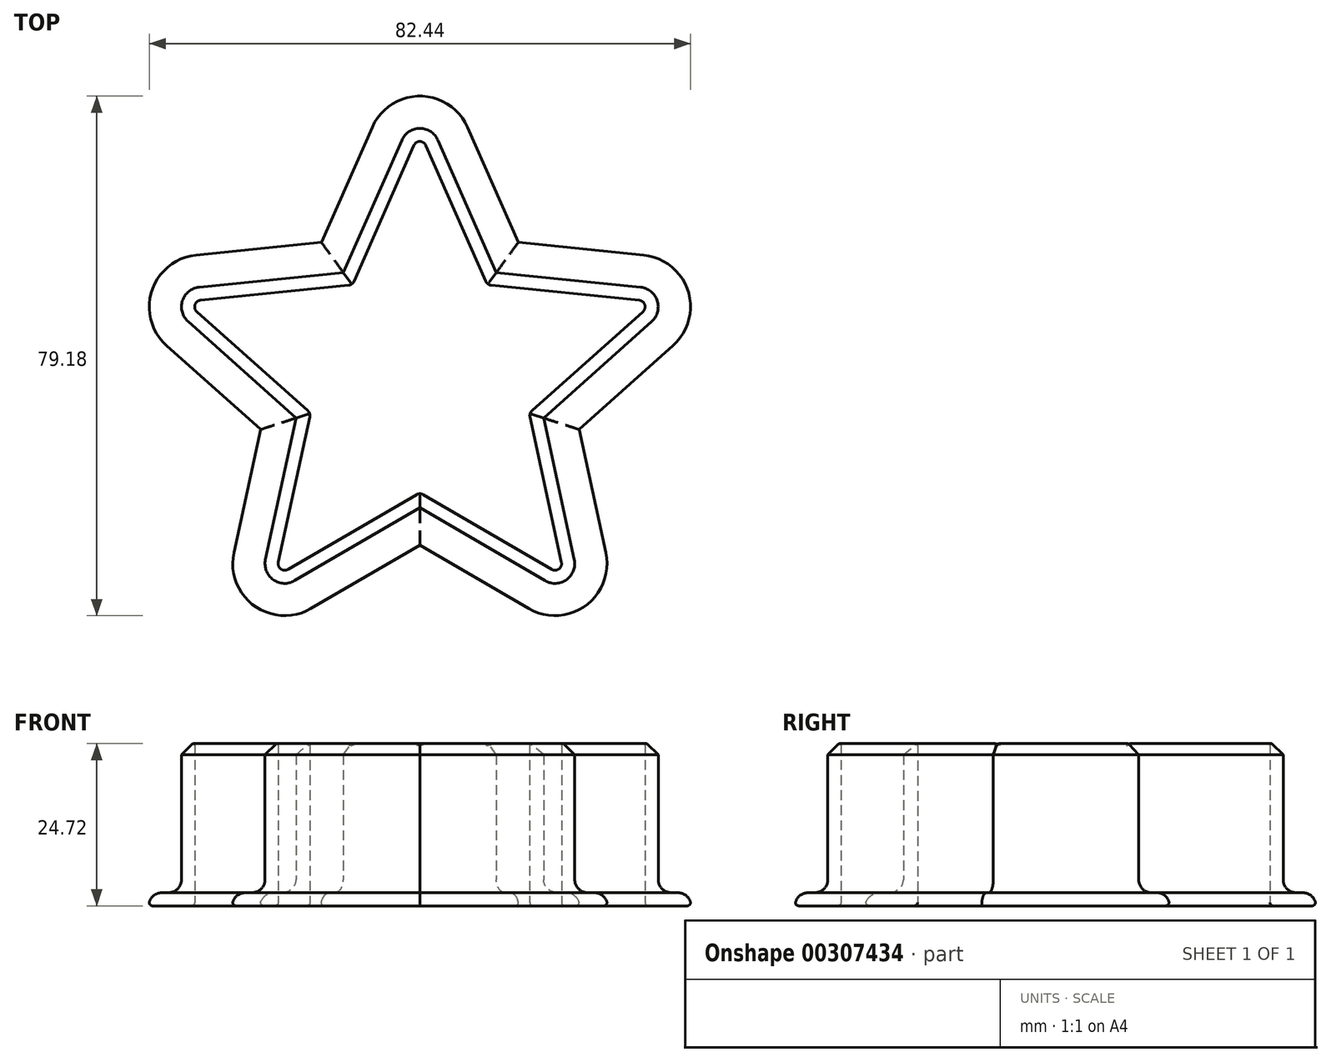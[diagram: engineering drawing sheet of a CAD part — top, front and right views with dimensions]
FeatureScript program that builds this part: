
annotation { "Feature Type Name" : "Feature", "Feature Type Description" : "" }
export const myFeature = defineFeature(function(context is Context, id is Id, definition is map)
    precondition{}
    {
        {
            var Q0;
            Q0=qCreatedBy(makeId("Top.planeOp"),FACE);
            var sketch = newSketch(context, id + "F0", { "sketchPlane" : qUnion([Q0])});
            skPoint(sketch, "E0.center", {"position": v(0, 0) * mm});
            skLineSegment(sketch, "E1", {"start": v(-0.92, 35.42) * mm, "end": v(-10.05, 14.7) * mm});
            skLineSegment(sketch, "E2", {"start": v(0.92, 35.42) * mm, "end": v(10.05, 14.7) * mm});
            skPoint(sketch, "E3.visualSharp", {"position": v(0, 37.5) * mm});
            skArc(sketch, "E3.filletArc", {"start": v(0.92, 35.42) * mm, "mid": v(0, 36.02) * mm, "end": v(-0.92, 35.42) * mm});
            skLineSegment(sketch, "E4.1.0", {"start": v(-33.97, 10.08) * mm, "end": v(-17.08, -5.02) * mm});
            skLineSegment(sketch, "E4.1.1", {"start": v(-33.4, 11.82) * mm, "end": v(-10.87, 14.1) * mm});
            skArc(sketch, "E4.1.2", {"start": v(-33.4, 11.82) * mm, "mid": v(-34.26, 11.13) * mm, "end": v(-33.97, 10.08) * mm});
            skLineSegment(sketch, "E4.2.0", {"start": v(-20.08, -29.2) * mm, "end": v(-0.5, -17.8) * mm});
            skLineSegment(sketch, "E4.2.1", {"start": v(-21.56, -28.12) * mm, "end": v(-16.77, -5.98) * mm});
            skArc(sketch, "E4.2.2", {"start": v(-21.56, -28.12) * mm, "mid": v(-21.17, -29.14) * mm, "end": v(-20.08, -29.2) * mm});
            skLineSegment(sketch, "E4.3.0", {"start": v(21.56, -28.12) * mm, "end": v(16.77, -5.98) * mm});
            skLineSegment(sketch, "E4.3.1", {"start": v(20.08, -29.2) * mm, "end": v(0.5, -17.8) * mm});
            skArc(sketch, "E4.3.2", {"start": v(20.08, -29.2) * mm, "mid": v(21.17, -29.14) * mm, "end": v(21.56, -28.12) * mm});
            skLineSegment(sketch, "E4.4.0", {"start": v(33.4, 11.82) * mm, "end": v(10.87, 14.1) * mm});
            skLineSegment(sketch, "E4.4.1", {"start": v(33.97, 10.08) * mm, "end": v(17.08, -5.02) * mm});
            skArc(sketch, "E4.4.2", {"start": v(33.97, 10.08) * mm, "mid": v(34.26, 11.13) * mm, "end": v(33.4, 11.82) * mm});
            skPoint(sketch, "E5.visualSharp", {"position": v(10.29, 14.16) * mm});
            skArc(sketch, "E5.filletArc", {"start": v(10.05, 14.7) * mm, "mid": v(10.38, 14.29) * mm, "end": v(10.87, 14.1) * mm});
            skPoint(sketch, "E6.visualSharp", {"position": v(-10.29, 14.16) * mm});
            skArc(sketch, "E6.filletArc", {"start": v(-10.87, 14.1) * mm, "mid": v(-10.38, 14.29) * mm, "end": v(-10.05, 14.7) * mm});
            skPoint(sketch, "E7.visualSharp", {"position": v(-16.64, -5.4) * mm});
            skArc(sketch, "E7.filletArc", {"start": v(-16.77, -5.98) * mm, "mid": v(-16.8, -5.46) * mm, "end": v(-17.08, -5.02) * mm});
            skPoint(sketch, "E8.visualSharp", {"position": v(0, -17.5) * mm});
            skArc(sketch, "E8.filletArc", {"start": v(0.5, -17.8) * mm, "mid": v(0, -17.66) * mm, "end": v(-0.5, -17.8) * mm});
            skPoint(sketch, "E9.visualSharp", {"position": v(16.64, -5.4) * mm});
            skArc(sketch, "E9.filletArc", {"start": v(17.08, -5.02) * mm, "mid": v(16.8, -5.46) * mm, "end": v(16.77, -5.98) * mm});
            skArc(sketch, "E10.0", {"start": v(2.75, 36.23) * mm, "mid": v(0, 38.02) * mm, "end": v(-2.75, 36.23) * mm});
            skLineSegment(sketch, "E10.1", {"start": v(-2.75, 36.23) * mm, "end": v(-11.65, 16.03) * mm});
            skLineSegment(sketch, "E10.2", {"start": v(-33.6, 13.8) * mm, "end": v(-11.65, 16.03) * mm});
            skArc(sketch, "E10.3", {"start": v(-33.6, 13.8) * mm, "mid": v(-36.16, 11.75) * mm, "end": v(-35.3, 8.58) * mm});
            skLineSegment(sketch, "E10.4", {"start": v(23.52, -27.7) * mm, "end": v(18.84, -6.12) * mm});
            skLineSegment(sketch, "E10.5", {"start": v(35.3, 8.58) * mm, "end": v(18.84, -6.12) * mm});
            skArc(sketch, "E10.6", {"start": v(35.3, 8.58) * mm, "mid": v(36.16, 11.75) * mm, "end": v(33.6, 13.8) * mm});
            skLineSegment(sketch, "E10.7", {"start": v(33.6, 13.8) * mm, "end": v(11.65, 16.03) * mm});
            skArc(sketch, "E10.8", {"start": v(19.07, -30.92) * mm, "mid": v(22.35, -30.76) * mm, "end": v(23.52, -27.7) * mm});
            skLineSegment(sketch, "E10.9", {"start": v(19.07, -30.92) * mm, "end": v(0, -19.81) * mm});
            skLineSegment(sketch, "E10.10", {"start": v(-19.07, -30.92) * mm, "end": v(0, -19.81) * mm});
            skArc(sketch, "E10.11", {"start": v(-23.52, -27.7) * mm, "mid": v(-22.35, -30.76) * mm, "end": v(-19.07, -30.92) * mm});
            skLineSegment(sketch, "E10.12", {"start": v(2.75, 36.23) * mm, "end": v(11.65, 16.03) * mm});
            skLineSegment(sketch, "E10.13", {"start": v(-23.52, -27.7) * mm, "end": v(-18.84, -6.12) * mm});
            skLineSegment(sketch, "E10.14", {"start": v(-35.3, 8.58) * mm, "end": v(-18.84, -6.12) * mm});
            skArc(sketch, "E11.0", {"start": v(7.32, 38.25) * mm, "mid": v(0, 43.02) * mm, "end": v(-7.32, 38.25) * mm});
            skLineSegment(sketch, "E11.1", {"start": v(-7.32, 38.25) * mm, "end": v(-15.05, 20.71) * mm});
            skLineSegment(sketch, "E11.2", {"start": v(-34.11, 18.78) * mm, "end": v(-15.05, 20.71) * mm});
            skArc(sketch, "E11.3", {"start": v(-34.11, 18.78) * mm, "mid": v(-40.91, 13.3) * mm, "end": v(-38.64, 4.86) * mm});
            skLineSegment(sketch, "E11.4", {"start": v(28.4, -26.64) * mm, "end": v(24.35, -7.91) * mm});
            skLineSegment(sketch, "E11.5", {"start": v(38.64, 4.86) * mm, "end": v(24.35, -7.91) * mm});
            skArc(sketch, "E11.6", {"start": v(38.64, 4.86) * mm, "mid": v(40.91, 13.3) * mm, "end": v(34.11, 18.78) * mm});
            skLineSegment(sketch, "E11.7", {"start": v(34.11, 18.78) * mm, "end": v(15.05, 20.71) * mm});
            skArc(sketch, "E11.8", {"start": v(16.56, -35.24) * mm, "mid": v(25.29, -34.8) * mm, "end": v(28.4, -26.64) * mm});
            skLineSegment(sketch, "E11.9", {"start": v(16.56, -35.24) * mm, "end": v(0, -25.6) * mm});
            skLineSegment(sketch, "E11.10", {"start": v(-16.56, -35.24) * mm, "end": v(0, -25.6) * mm});
            skArc(sketch, "E11.11", {"start": v(-28.4, -26.64) * mm, "mid": v(-25.29, -34.8) * mm, "end": v(-16.56, -35.24) * mm});
            skLineSegment(sketch, "E11.12", {"start": v(7.32, 38.25) * mm, "end": v(15.05, 20.71) * mm});
            skLineSegment(sketch, "E11.13", {"start": v(-28.4, -26.64) * mm, "end": v(-24.35, -7.91) * mm});
            skLineSegment(sketch, "E11.14", {"start": v(-38.64, 4.86) * mm, "end": v(-24.35, -7.91) * mm});
            skSolve(sketch);
        }
        {
            var Q0;
            Q0=makeQuery(id+"F0.imprint","IMPRINT",FACE,{"disambiguationData":[TD([[makeQuery(id+"F0.imprint","IMPRINT",EDGE,{"derivedFrom":sQuery(id+"F0.wireOp",EDGE,"E1")}),-1.0]])]});
            extrude(context, id + "F1", {"entities" : qUnion([Q0]), "depth" : 25 * mm});
        }
        {
            var Q0;
            Q0=makeQuery(id+"F0.imprint","IMPRINT",FACE,{"disambiguationData":[TD([[makeQuery(id+"F0.imprint","IMPRINT",EDGE,{"derivedFrom":sQuery(id+"F0.wireOp",EDGE,"E10.0")}),-1.0]])]});
            extrude(context, id + "F2", {"entities" : qUnion([Q0]), "operationType" : NewBodyOperationType.ADD, "depth" : 2 * mm});
        }
        {
            var Q0;
            Q0=makeQuery(id+"F1.opExtrude","CAP_EDGE",EDGE,{"disambiguationData":[OSD([sQuery(id+"F0.wireOp",EDGE,"E10.1")])],"isStart":false});
            var Q1;
            Q1=makeQuery(id+"F1.opExtrude","CAP_EDGE",EDGE,{"disambiguationData":[OSD([sQuery(id+"F0.wireOp",EDGE,"E10.7")])],"isStart":false});
            var Q2;
            Q2=makeQuery(id+"F1.opExtrude","CAP_EDGE",EDGE,{"disambiguationData":[OSD([sQuery(id+"F0.wireOp",EDGE,"E10.4")])],"isStart":false});
            var Q3;
            Q3=makeQuery(id+"F1.opExtrude","CAP_EDGE",EDGE,{"disambiguationData":[OSD([sQuery(id+"F0.wireOp",EDGE,"E10.10")])],"isStart":false});
            var Q4;
            Q4=makeQuery(id+"F1.opExtrude","CAP_EDGE",EDGE,{"disambiguationData":[OSD([sQuery(id+"F0.wireOp",EDGE,"E10.14")])],"isStart":false});
            chamfer(context, id + "F3", {"entities" : qUnion([Q0, Q1, Q2, Q3, Q4]), "width" : 2 * mm, "tangentPropagation" : true});
        }
        {
            var Q0;
            Q0=makeQuery(id+"F3.opChamfer","BLEND_EDGE",EDGE,{"blendedFrom":[makeQuery(id+"F1.opExtrude","CAP_EDGE",EDGE,{"disambiguationData":[OSD([sQuery(id+"F0.wireOp",EDGE,"E10.10")])],"isStart":false}),makeQuery(id+"F1.opExtrude","SWEPT_FACE",FACE,{"disambiguationData":[OSD([sQuery(id+"F0.wireOp",EDGE,"E4.2.0")])]})],"blendedInto":[makeQuery(id+"F1.opExtrude","SWEPT_FACE",FACE,{"disambiguationData":[OSD([sQuery(id+"F0.wireOp",EDGE,"E4.2.0")])]})]});
            var Q1;
            Q1=makeQuery(id+"F3.opChamfer","BLEND_EDGE",EDGE,{"blendedFrom":[makeQuery(id+"F1.opExtrude","CAP_EDGE",EDGE,{"disambiguationData":[OSD([sQuery(id+"F0.wireOp",EDGE,"E10.14")])],"isStart":false}),makeQuery(id+"F1.opExtrude","SWEPT_FACE",FACE,{"disambiguationData":[OSD([sQuery(id+"F0.wireOp",EDGE,"E4.1.0")])]})],"blendedInto":[makeQuery(id+"F1.opExtrude","SWEPT_FACE",FACE,{"disambiguationData":[OSD([sQuery(id+"F0.wireOp",EDGE,"E4.1.0")])]})]});
            var Q2;
            Q2=makeQuery(id+"F3.opChamfer","BLEND_EDGE",EDGE,{"blendedFrom":[makeQuery(id+"F1.opExtrude","CAP_EDGE",EDGE,{"disambiguationData":[OSD([sQuery(id+"F0.wireOp",EDGE,"E10.1")])],"isStart":false}),makeQuery(id+"F1.opExtrude","SWEPT_FACE",FACE,{"disambiguationData":[OSD([sQuery(id+"F0.wireOp",EDGE,"E1")])]})],"blendedInto":[makeQuery(id+"F1.opExtrude","SWEPT_FACE",FACE,{"disambiguationData":[OSD([sQuery(id+"F0.wireOp",EDGE,"E1")])]})]});
            var Q3;
            Q3=makeQuery(id+"F3.opChamfer","BLEND_EDGE",EDGE,{"blendedFrom":[makeQuery(id+"F1.opExtrude","CAP_EDGE",EDGE,{"disambiguationData":[OSD([sQuery(id+"F0.wireOp",EDGE,"E10.5")])],"isStart":false}),makeQuery(id+"F1.opExtrude","SWEPT_FACE",FACE,{"disambiguationData":[OSD([sQuery(id+"F0.wireOp",EDGE,"E4.4.1")])]})],"blendedInto":[makeQuery(id+"F1.opExtrude","SWEPT_FACE",FACE,{"disambiguationData":[OSD([sQuery(id+"F0.wireOp",EDGE,"E4.4.1")])]})]});
            var Q4;
            Q4=makeQuery(id+"F3.opChamfer","BLEND_EDGE",EDGE,{"blendedFrom":[makeQuery(id+"F1.opExtrude","CAP_EDGE",EDGE,{"disambiguationData":[OSD([sQuery(id+"F0.wireOp",EDGE,"E10.4")])],"isStart":false}),makeQuery(id+"F1.opExtrude","SWEPT_FACE",FACE,{"disambiguationData":[OSD([sQuery(id+"F0.wireOp",EDGE,"E4.3.0")])]})],"blendedInto":[makeQuery(id+"F1.opExtrude","SWEPT_FACE",FACE,{"disambiguationData":[OSD([sQuery(id+"F0.wireOp",EDGE,"E4.3.0")])]})]});
            fillet(context, id + "F4", {"entities" : qUnion([Q0, Q1, Q2, Q3, Q4]), "radius" : .2 * mm, "tangentPropagation" : true, "allowEdgeOverflow" : false});
        }
        {
            var Q0;
            Q0=makeQuery(id+"F2.opExtrude","CAP_FACE",FACE,{"disambiguationData":[OSD([sQuery(id+"F0.wireOp",EDGE,"E10.0"),sQuery(id+"F0.wireOp",EDGE,"E10.1"),sQuery(id+"F0.wireOp",EDGE,"E10.2"),sQuery(id+"F0.wireOp",EDGE,"E10.3"),sQuery(id+"F0.wireOp",EDGE,"E10.4"),sQuery(id+"F0.wireOp",EDGE,"E10.5"),sQuery(id+"F0.wireOp",EDGE,"E10.6"),sQuery(id+"F0.wireOp",EDGE,"E10.7"),sQuery(id+"F0.wireOp",EDGE,"E10.8"),sQuery(id+"F0.wireOp",EDGE,"E10.9"),sQuery(id+"F0.wireOp",EDGE,"E10.10"),sQuery(id+"F0.wireOp",EDGE,"E10.11"),sQuery(id+"F0.wireOp",EDGE,"E10.12"),sQuery(id+"F0.wireOp",EDGE,"E10.13"),sQuery(id+"F0.wireOp",EDGE,"E10.14"),sQuery(id+"F0.wireOp",EDGE,"E11.0"),sQuery(id+"F0.wireOp",EDGE,"E11.1"),sQuery(id+"F0.wireOp",EDGE,"E11.2"),sQuery(id+"F0.wireOp",EDGE,"E11.3"),sQuery(id+"F0.wireOp",EDGE,"E11.4"),sQuery(id+"F0.wireOp",EDGE,"E11.5"),sQuery(id+"F0.wireOp",EDGE,"E11.6"),sQuery(id+"F0.wireOp",EDGE,"E11.7"),sQuery(id+"F0.wireOp",EDGE,"E11.8"),sQuery(id+"F0.wireOp",EDGE,"E11.9"),sQuery(id+"F0.wireOp",EDGE,"E11.10"),sQuery(id+"F0.wireOp",EDGE,"E11.11"),sQuery(id+"F0.wireOp",EDGE,"E11.12"),sQuery(id+"F0.wireOp",EDGE,"E11.13"),sQuery(id+"F0.wireOp",EDGE,"E11.14")])],"isStart":false});
            fillet(context, id + "F5", {"entities" : qUnion([Q0]), "radius" : 2 * mm, "tangentPropagation" : true, "allowEdgeOverflow" : false});
        }
        {
            var Q0;
            {var subQ0=sQuery(id+"F0.wireOp",EDGE,"E10.14");var subQ1=sQuery(id+"F0.wireOp",EDGE,"E10.13");var subQ2=sQuery(id+"F0.wireOp",EDGE,"E10.12");var subQ3=sQuery(id+"F0.wireOp",EDGE,"E10.11");var subQ4=sQuery(id+"F0.wireOp",EDGE,"E10.10");var subQ5=sQuery(id+"F0.wireOp",EDGE,"E10.9");var subQ6=sQuery(id+"F0.wireOp",EDGE,"E10.8");var subQ7=sQuery(id+"F0.wireOp",EDGE,"E10.7");var subQ8=sQuery(id+"F0.wireOp",EDGE,"E10.6");var subQ9=sQuery(id+"F0.wireOp",EDGE,"E10.5");var subQ10=sQuery(id+"F0.wireOp",EDGE,"E10.4");var subQ11=sQuery(id+"F0.wireOp",EDGE,"E10.3");var subQ12=sQuery(id+"F0.wireOp",EDGE,"E10.2");var subQ13=sQuery(id+"F0.wireOp",EDGE,"E10.1");var subQ14=sQuery(id+"F0.wireOp",EDGE,"E10.0");Q0=makeQuery(id+"F2.boolean.opBoolean","MERGE",FACE,{"derivedFrom":[makeQuery(id+"F1.opExtrude","CAP_FACE",FACE,{"disambiguationData":[OSD([sQuery(id+"F0.wireOp",EDGE,"E1"),sQuery(id+"F0.wireOp",EDGE,"E2"),sQuery(id+"F0.wireOp",EDGE,"E3.filletArc"),sQuery(id+"F0.wireOp",EDGE,"E4.1.0"),sQuery(id+"F0.wireOp",EDGE,"E4.1.1"),sQuery(id+"F0.wireOp",EDGE,"E4.1.2"),sQuery(id+"F0.wireOp",EDGE,"E4.2.0"),sQuery(id+"F0.wireOp",EDGE,"E4.2.1"),sQuery(id+"F0.wireOp",EDGE,"E4.2.2"),sQuery(id+"F0.wireOp",EDGE,"E4.3.0"),sQuery(id+"F0.wireOp",EDGE,"E4.3.1"),sQuery(id+"F0.wireOp",EDGE,"E4.3.2"),sQuery(id+"F0.wireOp",EDGE,"E4.4.0"),sQuery(id+"F0.wireOp",EDGE,"E4.4.1"),sQuery(id+"F0.wireOp",EDGE,"E4.4.2"),sQuery(id+"F0.wireOp",EDGE,"E5.filletArc"),sQuery(id+"F0.wireOp",EDGE,"E6.filletArc"),sQuery(id+"F0.wireOp",EDGE,"E7.filletArc"),sQuery(id+"F0.wireOp",EDGE,"E8.filletArc"),sQuery(id+"F0.wireOp",EDGE,"E9.filletArc"),subQ14,subQ13,subQ12,subQ11,subQ10,subQ9,subQ8,subQ7,subQ6,subQ5,subQ4,subQ3,subQ2,subQ1,subQ0])],"isStart":true}),makeQuery(id+"F2.opExtrude","CAP_FACE",FACE,{"disambiguationData":[OSD([subQ14,subQ13,subQ12,subQ11,subQ10,subQ9,subQ8,subQ7,subQ6,subQ5,subQ4,subQ3,subQ2,subQ1,subQ0,sQuery(id+"F0.wireOp",EDGE,"E11.0"),sQuery(id+"F0.wireOp",EDGE,"E11.1"),sQuery(id+"F0.wireOp",EDGE,"E11.2"),sQuery(id+"F0.wireOp",EDGE,"E11.3"),sQuery(id+"F0.wireOp",EDGE,"E11.4"),sQuery(id+"F0.wireOp",EDGE,"E11.5"),sQuery(id+"F0.wireOp",EDGE,"E11.6"),sQuery(id+"F0.wireOp",EDGE,"E11.7"),sQuery(id+"F0.wireOp",EDGE,"E11.8"),sQuery(id+"F0.wireOp",EDGE,"E11.9"),sQuery(id+"F0.wireOp",EDGE,"E11.10"),sQuery(id+"F0.wireOp",EDGE,"E11.11"),sQuery(id+"F0.wireOp",EDGE,"E11.12"),sQuery(id+"F0.wireOp",EDGE,"E11.13"),sQuery(id+"F0.wireOp",EDGE,"E11.14")])],"isStart":true})]});}
            fillet(context, id + "F6", {"entities" : qUnion([Q0]), "radius" : .5 * mm, "tangentPropagation" : true, "allowEdgeOverflow" : false});
        }
    });
